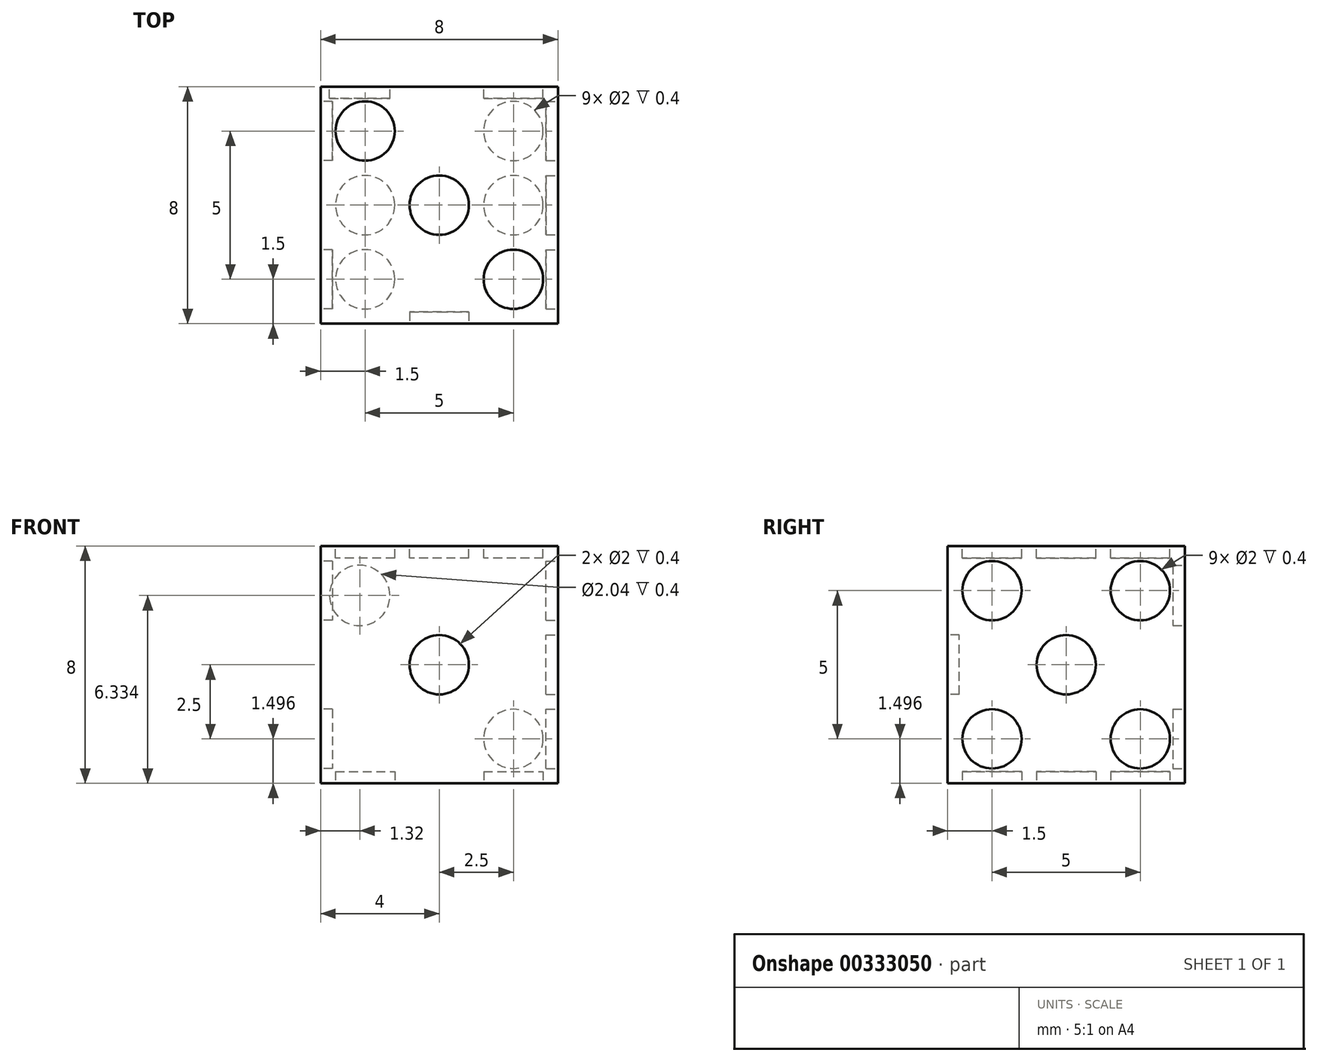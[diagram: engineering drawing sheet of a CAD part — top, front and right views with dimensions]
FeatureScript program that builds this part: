
annotation { "Feature Type Name" : "Feature", "Feature Type Description" : "" }
export const myFeature = defineFeature(function(context is Context, id is Id, definition is map)
    precondition{}
    {
        {
            var Q0;
            Q0=qCreatedBy(makeId("Front.planeOp"),FACE);
            var sketch = newSketch(context, id + "F0", { "sketchPlane" : qUnion([Q0])});
            skLineSegment(sketch, "E0.bottom", {"start": v(-1.96, 8.23) * mm, "end": v(6.04, 8.23) * mm});
            skLineSegment(sketch, "E0.top", {"start": v(-1.96, 0.23) * mm, "end": v(6.04, 0.23) * mm});
            skLineSegment(sketch, "E0.left", {"start": v(-1.96, 8.23) * mm, "end": v(-1.96, 0.23) * mm});
            skLineSegment(sketch, "E0.right", {"start": v(6.04, 8.23) * mm, "end": v(6.04, 0.23) * mm});
            skSolve(sketch);
        }
        {
            var Q0;
            Q0 = qSketchRegion(id + "F0", true);
            extrude(context, id + "F1", {"entities" : qUnion([Q0]), "depth" : 8 * mm});
        }
        {
            var Q0;
            Q0=makeQuery(id+"F1.opExtrude","CAP_FACE",FACE,{"disambiguationData":[OSD([sQuery(id+"F0.wireOp",EDGE,"E0.bottom"),sQuery(id+"F0.wireOp",EDGE,"E0.top"),sQuery(id+"F0.wireOp",EDGE,"E0.left"),sQuery(id+"F0.wireOp",EDGE,"E0.right")])],"isStart":false});
            var sketch = newSketch(context, id + "F2", { "sketchPlane" : qUnion([Q0])});
            skCircle(sketch, "E1", {"center": v(2.04, 4.23) * mm, "radius": 1 * mm});
            skSolve(sketch);
        }
        {
            var Q0;
            Q0=makeQuery(id+"F2.imprint","IMPRINT",FACE,{"disambiguationData":[TD([[makeQuery(id+"F2.imprint","IMPRINT",EDGE,{"derivedFrom":sQuery(id+"F2.wireOp",EDGE,"E1")}),1.0]])]});
            extrude(context, id + "F3", {"entities" : qUnion([Q0]), "operationType" : NewBodyOperationType.REMOVE, "oppositeDirection" : true, "depth" : .4 * mm});
        }
        {
            var Q0;
            Q0=makeQuery(id+"F1.opExtrude","CAP_FACE",FACE,{"disambiguationData":[OSD([sQuery(id+"F0.wireOp",EDGE,"E0.bottom"),sQuery(id+"F0.wireOp",EDGE,"E0.top"),sQuery(id+"F0.wireOp",EDGE,"E0.left"),sQuery(id+"F0.wireOp",EDGE,"E0.right")])],"isStart":true});
            var sketch = newSketch(context, id + "F4", { "sketchPlane" : qUnion([Q0])});
            skCircle(sketch, "E2", {"center": v(-4.54, 1.73) * mm, "radius": 1 * mm});
            skCircle(sketch, "E3", {"center": v(0.64, 6.56) * mm, "radius": 1.02 * mm});
            skSolve(sketch);
        }
        {
            var Q0;
            Q0=makeQuery(id+"F4.imprint","IMPRINT",FACE,{"disambiguationData":[TD([[makeQuery(id+"F4.imprint","IMPRINT",EDGE,{"derivedFrom":sQuery(id+"F4.wireOp",EDGE,"E2")}),1.0]])]});
            var Q1;
            Q1=makeQuery(id+"F4.imprint","IMPRINT",FACE,{"disambiguationData":[TD([[makeQuery(id+"F4.imprint","IMPRINT",EDGE,{"derivedFrom":sQuery(id+"F4.wireOp",EDGE,"E3")}),1.0]])]});
            extrude(context, id + "F5", {"entities" : qUnion([Q0, Q1]), "operationType" : NewBodyOperationType.REMOVE, "oppositeDirection" : true, "depth" : .4 * mm});
        }
        {
            var Q0;
            Q0=makeQuery(id+"F1.opExtrude","SWEPT_FACE",FACE,{"disambiguationData":[OSD([sQuery(id+"F0.wireOp",EDGE,"E0.left")])]});
            var sketch = newSketch(context, id + "F6", { "sketchPlane" : qUnion([Q0])});
            skCircle(sketch, "E4", {"center": v(6.5, 6.73) * mm, "radius": 1 * mm});
            skCircle(sketch, "E5", {"center": v(1.5, 1.73) * mm, "radius": 1 * mm});
            skCircle(sketch, "E6", {"center": v(1.5, 6.73) * mm, "radius": 1 * mm});
            skCircle(sketch, "E7", {"center": v(6.5, 1.73) * mm, "radius": 1 * mm});
            skSolve(sketch);
        }
        {
            var Q0;
            Q0=makeQuery(id+"F6.imprint","IMPRINT",FACE,{"disambiguationData":[TD([[makeQuery(id+"F6.imprint","IMPRINT",EDGE,{"derivedFrom":sQuery(id+"F6.wireOp",EDGE,"E4")}),1.0]])]});
            var Q1;
            Q1=makeQuery(id+"F6.imprint","IMPRINT",FACE,{"disambiguationData":[TD([[makeQuery(id+"F6.imprint","IMPRINT",EDGE,{"derivedFrom":sQuery(id+"F6.wireOp",EDGE,"E6")}),1.0]])]});
            var Q2;
            Q2=makeQuery(id+"F6.imprint","IMPRINT",FACE,{"disambiguationData":[TD([[makeQuery(id+"F6.imprint","IMPRINT",EDGE,{"derivedFrom":sQuery(id+"F6.wireOp",EDGE,"E5")}),1.0]])]});
            var Q3;
            Q3=makeQuery(id+"F6.imprint","IMPRINT",FACE,{"disambiguationData":[TD([[makeQuery(id+"F6.imprint","IMPRINT",EDGE,{"derivedFrom":sQuery(id+"F6.wireOp",EDGE,"E7")}),1.0]])]});
            extrude(context, id + "F7", {"entities" : qUnion([Q0, Q1, Q2, Q3]), "operationType" : NewBodyOperationType.REMOVE, "oppositeDirection" : true, "depth" : .4 * mm});
        }
        {
            var Q0;
            Q0=makeQuery(id+"F1.opExtrude","SWEPT_FACE",FACE,{"disambiguationData":[OSD([sQuery(id+"F0.wireOp",EDGE,"E0.right")])]});
            var sketch = newSketch(context, id + "F8", { "sketchPlane" : qUnion([Q0])});
            skCircle(sketch, "E8", {"center": v(-4, 4.23) * mm, "radius": 1 * mm});
            skCircle(sketch, "E9", {"center": v(-1.5, 6.73) * mm, "radius": 1 * mm});
            skCircle(sketch, "E10", {"center": v(-6.5, 1.73) * mm, "radius": 1 * mm});
            skCircle(sketch, "E11", {"center": v(-6.5, 6.73) * mm, "radius": 1 * mm});
            skCircle(sketch, "E12", {"center": v(-1.5, 1.73) * mm, "radius": 1 * mm});
            skSolve(sketch);
        }
        {
            var Q0;
            Q0=makeQuery(id+"F8.imprint","IMPRINT",FACE,{"disambiguationData":[TD([[makeQuery(id+"F8.imprint","IMPRINT",EDGE,{"derivedFrom":sQuery(id+"F8.wireOp",EDGE,"E8")}),1.0]])]});
            var Q1;
            Q1=makeQuery(id+"F8.imprint","IMPRINT",FACE,{"disambiguationData":[TD([[makeQuery(id+"F8.imprint","IMPRINT",EDGE,{"derivedFrom":sQuery(id+"F8.wireOp",EDGE,"E11")}),1.0]])]});
            var Q2;
            Q2=makeQuery(id+"F8.imprint","IMPRINT",FACE,{"disambiguationData":[TD([[makeQuery(id+"F8.imprint","IMPRINT",EDGE,{"derivedFrom":sQuery(id+"F8.wireOp",EDGE,"E9")}),1.0]])]});
            var Q3;
            Q3=makeQuery(id+"F8.imprint","IMPRINT",FACE,{"disambiguationData":[TD([[makeQuery(id+"F8.imprint","IMPRINT",EDGE,{"derivedFrom":sQuery(id+"F8.wireOp",EDGE,"E12")}),1.0]])]});
            var Q4;
            Q4=makeQuery(id+"F8.imprint","IMPRINT",FACE,{"disambiguationData":[TD([[makeQuery(id+"F8.imprint","IMPRINT",EDGE,{"derivedFrom":sQuery(id+"F8.wireOp",EDGE,"E10")}),1.0]])]});
            extrude(context, id + "F9", {"entities" : qUnion([Q0, Q1, Q2, Q3, Q4]), "operationType" : NewBodyOperationType.REMOVE, "oppositeDirection" : true, "depth" : .4 * mm});
        }
        {
            var Q0;
            Q0=makeQuery(id+"F1.opExtrude","SWEPT_FACE",FACE,{"disambiguationData":[OSD([sQuery(id+"F0.wireOp",EDGE,"E0.bottom")])]});
            var sketch = newSketch(context, id + "F10", { "sketchPlane" : qUnion([Q0])});
            skCircle(sketch, "E13", {"center": v(-0.46, -1.5) * mm, "radius": 1 * mm});
            skCircle(sketch, "E14", {"center": v(2.04, -4) * mm, "radius": 1 * mm});
            skCircle(sketch, "E15", {"center": v(4.54, -6.5) * mm, "radius": 1 * mm});
            skSolve(sketch);
        }
        {
            var Q0;
            Q0=makeQuery(id+"F10.imprint","IMPRINT",FACE,{"disambiguationData":[TD([[makeQuery(id+"F10.imprint","IMPRINT",EDGE,{"derivedFrom":sQuery(id+"F10.wireOp",EDGE,"E13")}),1.0]])]});
            var Q1;
            Q1=makeQuery(id+"F10.imprint","IMPRINT",FACE,{"disambiguationData":[TD([[makeQuery(id+"F10.imprint","IMPRINT",EDGE,{"derivedFrom":sQuery(id+"F10.wireOp",EDGE,"E14")}),1.0]])]});
            var Q2;
            Q2=makeQuery(id+"F10.imprint","IMPRINT",FACE,{"disambiguationData":[TD([[makeQuery(id+"F10.imprint","IMPRINT",EDGE,{"derivedFrom":sQuery(id+"F10.wireOp",EDGE,"E15")}),1.0]])]});
            extrude(context, id + "F11", {"entities" : qUnion([Q0, Q1, Q2]), "operationType" : NewBodyOperationType.REMOVE, "oppositeDirection" : true, "depth" : .4 * mm});
        }
        {
            var Q0;
            Q0=makeQuery(id+"F1.opExtrude","SWEPT_FACE",FACE,{"disambiguationData":[OSD([sQuery(id+"F0.wireOp",EDGE,"E0.top")])]});
            var sketch = newSketch(context, id + "F12", { "sketchPlane" : qUnion([Q0])});
            skCircle(sketch, "E16", {"center": v(-0.46, 6.5) * mm, "radius": 1 * mm});
            skCircle(sketch, "E17", {"center": v(-0.46, 4) * mm, "radius": 1 * mm});
            skCircle(sketch, "E18", {"center": v(-0.46, 1.5) * mm, "radius": 1 * mm});
            skCircle(sketch, "E19", {"center": v(4.54, 6.5) * mm, "radius": 1 * mm});
            skCircle(sketch, "E20", {"center": v(4.54, 4) * mm, "radius": 1 * mm});
            skCircle(sketch, "E21", {"center": v(4.54, 1.5) * mm, "radius": 1 * mm});
            skSolve(sketch);
        }
        {
            var Q0;
            Q0=makeQuery(id+"F12.imprint","IMPRINT",FACE,{"disambiguationData":[TD([[makeQuery(id+"F12.imprint","IMPRINT",EDGE,{"derivedFrom":sQuery(id+"F12.wireOp",EDGE,"E16")}),1.0]])]});
            var Q1;
            Q1=makeQuery(id+"F12.imprint","IMPRINT",FACE,{"disambiguationData":[TD([[makeQuery(id+"F12.imprint","IMPRINT",EDGE,{"derivedFrom":sQuery(id+"F12.wireOp",EDGE,"E17")}),1.0]])]});
            var Q2;
            Q2=makeQuery(id+"F12.imprint","IMPRINT",FACE,{"disambiguationData":[TD([[makeQuery(id+"F12.imprint","IMPRINT",EDGE,{"derivedFrom":sQuery(id+"F12.wireOp",EDGE,"E18")}),1.0]])]});
            var Q3;
            Q3=makeQuery(id+"F12.imprint","IMPRINT",FACE,{"disambiguationData":[TD([[makeQuery(id+"F12.imprint","IMPRINT",EDGE,{"derivedFrom":sQuery(id+"F12.wireOp",EDGE,"E21")}),1.0]])]});
            var Q4;
            Q4=makeQuery(id+"F12.imprint","IMPRINT",FACE,{"disambiguationData":[TD([[makeQuery(id+"F12.imprint","IMPRINT",EDGE,{"derivedFrom":sQuery(id+"F12.wireOp",EDGE,"E20")}),1.0]])]});
            var Q5;
            Q5=makeQuery(id+"F12.imprint","IMPRINT",FACE,{"disambiguationData":[TD([[makeQuery(id+"F12.imprint","IMPRINT",EDGE,{"derivedFrom":sQuery(id+"F12.wireOp",EDGE,"E19")}),1.0]])]});
            extrude(context, id + "F13", {"entities" : qUnion([Q0, Q1, Q2, Q3, Q4, Q5]), "operationType" : NewBodyOperationType.REMOVE, "oppositeDirection" : true, "depth" : .4 * mm});
        }
    });
